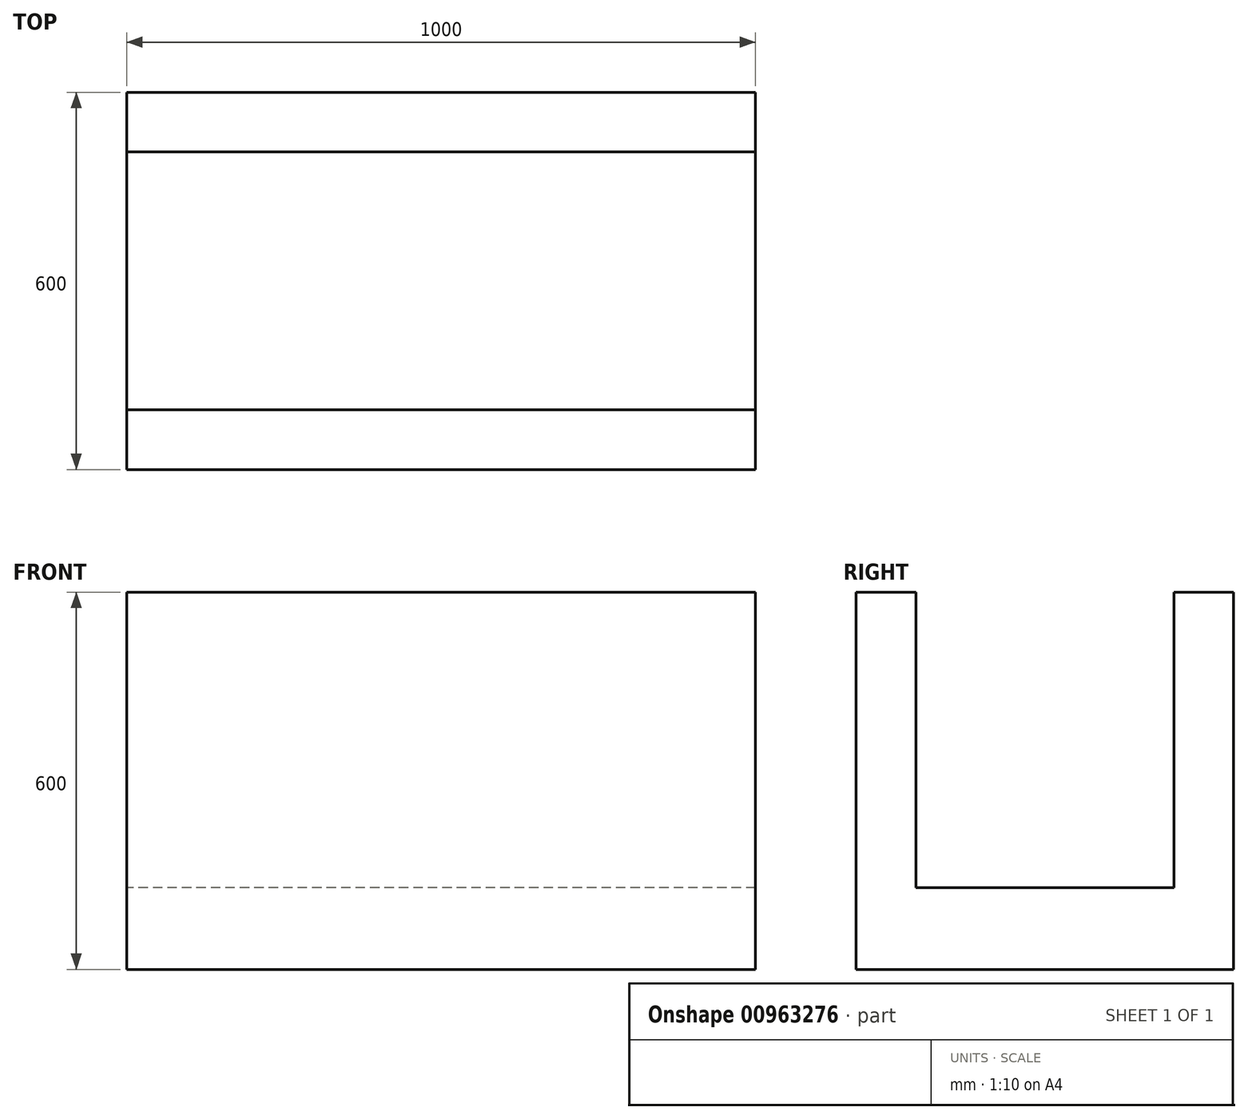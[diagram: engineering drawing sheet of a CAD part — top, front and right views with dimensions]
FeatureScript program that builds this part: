
annotation { "Feature Type Name" : "Feature", "Feature Type Description" : "" }
export const myFeature = defineFeature(function(context is Context, id is Id, definition is map)
    precondition{}
    {
        {
            var Q0;
            Q0=qCreatedBy(makeId("Right.planeOp"),FACE);
            var sketch = newSketch(context, id + "F0", { "sketchPlane" : qUnion([Q0])});
            skLineSegment(sketch, "E0.bottom", {"start": v(-299.17, 364.52) * mm, "end": v(300.83, 364.52) * mm});
            skLineSegment(sketch, "E0.top", {"start": v(-299.17, -235.48) * mm, "end": v(300.83, -235.48) * mm});
            skLineSegment(sketch, "E0.left", {"start": v(-299.17, 364.52) * mm, "end": v(-299.17, -235.48) * mm});
            skLineSegment(sketch, "E0.right", {"start": v(300.83, 364.52) * mm, "end": v(300.83, -235.48) * mm});
            skLineSegment(sketch, "E1", {"start": v(-204.17, 364.52) * mm, "end": v(-204.17, -105.48) * mm});
            skLineSegment(sketch, "E2", {"start": v(-204.17, -105.48) * mm, "end": v(205.83, -105.48) * mm});
            skLineSegment(sketch, "E3", {"start": v(205.83, -105.48) * mm, "end": v(205.83, 364.52) * mm});
            skSolve(sketch);
        }
        {
            var Q0;
            Q0=makeQuery(id+"F0.imprint","IMPRINT",FACE,{"disambiguationData":[TD([[makeQuery(id+"F0.imprint","IMPRINT",EDGE,{"derivedFrom":sQuery(id+"F0.wireOp",EDGE,"E0.top")}),1.0]])]});
            extrude(context, id + "F1", {"entities" : qUnion([Q0]), "depth" : 1000 * mm, "offsetDistance" : 25 * mm, "hasSecondDirectionOffset" : true, "secondDirectionOffsetDistance" : 1000 * mm});
        }
    });
